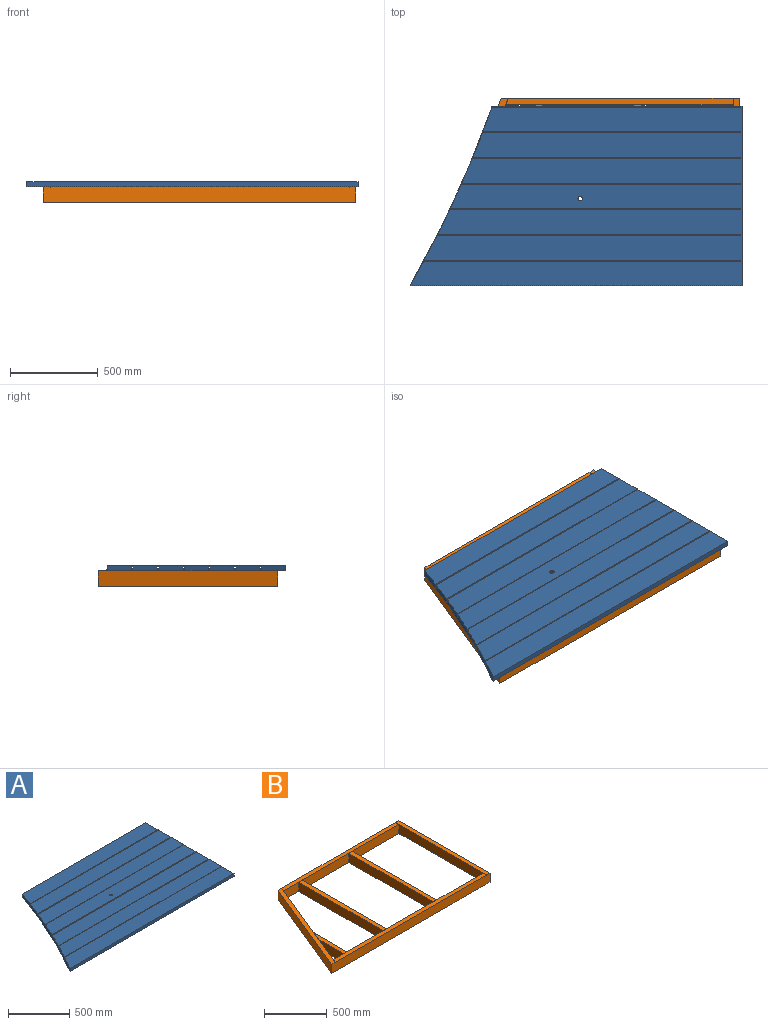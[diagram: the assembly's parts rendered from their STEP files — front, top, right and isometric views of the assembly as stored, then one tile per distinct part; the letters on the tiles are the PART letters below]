
ASSEMBLY  parts=2 mates=1
PART A: 33 faces, bbox 1890x1022.4x29.4 mm
  f0: cylinder r=6096mm len=1022.35mm, axis (0,0,-1), area 31985.5mm2, adj f1,f3,f4,f5,f6,f7,f8,f9
  f1: plane 1890x1022.35mm, normal (0,0,-1), area 1673082.8mm2, adj f0,f2,f10,f31,f32
  f2: plane 1022.35x29.37mm, normal (1,0,0), area 29037.2mm2, adj f1,f3,f4,f5,f6,f7,f8,f9
  f3: plane 1475.36x139.7mm, normal (0,0,1), area 202498.6mm2, adj f0,f2,f28,f30
  f4: plane 1532.89x139.7mm, normal (0,0,1), area 210247.9mm2, adj f0,f2,f25,f27
  f5: plane 1594.83x139.7mm, normal (0,0,1), area 218604.7mm2, adj f0,f2,f22,f24
  f6: plane 1661.33x139.7mm, normal (0,0,1), area 227082mm2, adj f0,f2,f19,f21,f32
  f7: plane 1732.57x139.7mm, normal (0,0,1), area 237222mm2, adj f0,f2,f16,f18
  f8: plane 1808.72x139.7mm, normal (0,0,1), area 247529.5mm2, adj f0,f2,f13,f15
  f9: plane 1890x139.7mm, normal (0,0,1), area 258539.2mm2, adj f0,f2,f10,f12
  f10: plane 1890x29.37mm, normal (0,-1,0), area 55507mm2, adj f0,f1,f2,f9
  f11: plane 1812.15x6.35mm, normal (0,0,1), area 11496.2mm2, adj f0,f2,f12,f13
  f12: plane 1812.15x22.23mm, normal (0,1,0), area 40274.9mm2, adj f0,f2,f9,f11
  f13: plane 1808.72x22.23mm, normal (0,-1,0), area 40198.8mm2, adj f0,f2,f8,f11
  f14: plane 1735.78x6.35mm, normal (0,0,1), area 11012mm2, adj f0,f2,f15,f16
  f15: plane 1735.78x22.23mm, normal (0,1,0), area 38577.6mm2, adj f0,f2,f8,f14
  f16: plane 1732.57x22.23mm, normal (0,-1,0), area 38506.3mm2, adj f0,f2,f7,f14
  f17: plane 1664.33x6.35mm, normal (0,0,1), area 10559mm2, adj f0,f2,f18,f19
  f18: plane 1664.33x22.23mm, normal (0,1,0), area 36989.8mm2, adj f0,f2,f7,f17
  f19: plane 1661.33x22.23mm, normal (0,-1,0), area 36923.1mm2, adj f0,f2,f6,f17
  f20: plane 1597.62x6.35mm, normal (0,0,1), area 10136mm2, adj f0,f2,f21,f22
  f21: plane 1597.62x22.23mm, normal (0,1,0), area 35507.2mm2, adj f0,f2,f6,f20
  f22: plane 1594.83x22.23mm, normal (0,-1,0), area 35445.1mm2, adj f0,f2,f5,f20
  f23: plane 1535.49x6.35mm, normal (0,0,1), area 9742.1mm2, adj f0,f2,f24,f25
  f24: plane 1535.49x22.23mm, normal (0,1,0), area 34126.2mm2, adj f0,f2,f5,f23
  f25: plane 1532.89x22.23mm, normal (0,-1,0), area 34068.4mm2, adj f0,f2,f4,f23
  f26: plane 1477.77x6.35mm, normal (0,0,1), area 9376.2mm2, adj f0,f2,f27,f28
  f27: plane 1477.77x22.23mm, normal (0,1,0), area 32843.4mm2, adj f0,f2,f4,f26
  f28: plane 1475.36x22.23mm, normal (0,-1,0), area 32789.8mm2, adj f0,f2,f3,f26
  f29: plane 1424.34x6.35mm, normal (0,0,1), area 9037.5mm2, adj f0,f2,f30,f31
  f30: plane 1424.34x22.23mm, normal (0,1,0), area 31655.9mm2, adj f0,f2,f3,f29
  f31: plane 1422.11x7.14mm, normal (0,1,0), area 10159.2mm2, adj f0,f1,f2,f29
  f32: cylinder r=12.7mm len=29.37mm, axis (0,0,1), area 2343.5mm2, adj f1,f6
PART B: 42 faces, bbox 1778x1022.4x88.9 mm
  f0: plane 1358.9x88.9mm, normal (0,1,0), area 120806.1mm2, adj f10,f11,f12,f13,f15,f17,f19,f21
  f1: plane 1295.24x88.9mm, normal (0,-1,0), area 108566.2mm2, adj f2,f3,f4,f6,f10,f15,f17,f21
  f2: plane 946.15x88.9mm, normal (-1,0,0), area 84112.6mm2, adj f1,f8,f16,f21,f24,f25,f26,f27
  f3: plane 946.15x88.9mm, normal (-1,0,0), area 84112.6mm2, adj f1,f9,f16,f21,f34,f35,f36,f37
  f4: plane 946.15x88.9mm, normal (1,0,0), area 84112.6mm2, adj f1,f9,f16,f21,f34,f35,f36,f37
  f5: plane 367.55x88.9mm, normal (1,0,0), area 32674.7mm2, adj f7,f15,f16,f21,f28,f29,f30,f31
  f6: plane 946.15x88.9mm, normal (1,0,0), area 84112.6mm2, adj f1,f8,f16,f21,f24,f25,f26,f27
  f7: plane 367.45x38.1mm, normal (0,0,1), area 12229.5mm2, adj f5,f18,f29,f31
  f8: plane 946.1x38.1mm, normal (0,0,1), area 36046.4mm2, adj f2,f6,f25,f27
  f9: plane 946.1x38.1mm, normal (0,0,1), area 36046.4mm2, adj f3,f4,f35,f37
  f10: plane 1295.19x38.1mm, normal (0,0,1), area 49049.2mm2, adj f0,f1,f33,f41
  f11: plane 1022.35x460.28mm, normal (0,0,1), area 42097.4mm2, adj f0,f13,f14,f15
  f12: plane 1022.35x38.1mm, normal (0,0,1), area 38951.5mm2, adj f0,f14,f17,f19
  f13: plane 1022.35x419.1mm, normal (-0.93,0.38,0), area 98227.2mm2, adj f0,f11,f14,f21
  f14: plane 1778x88.9mm, normal (0,-1,0), area 158064.1mm2, adj f11,f12,f13,f15,f17,f19,f20,f21
  f15: plane 1022.35x419.1mm, normal (0.93,-0.38,0), area 82440.5mm2, adj f0,f1,f5,f11,f14,f16,f18,f21
  f16: plane 1683.1x88.9mm, normal (0,1,0), area 139756.9mm2, adj f2,f3,f4,f5,f6,f15,f17,f18
  f17: plane 1022.35x88.9mm, normal (-1,0,0), area 84306.3mm2, adj f0,f1,f12,f14,f16,f21,f22,f32
  f18: plane 274.61x88.9mm, normal (-1,0,0), area 24412.2mm2, adj f7,f15,f16,f21,f28,f29,f30,f31
  f19: plane 1022.35x88.9mm, normal (1,0,0), area 90886.9mm2, adj f0,f12,f14,f21
  f20: plane 1698.67x38.1mm, normal (0,0,1), area 64421.8mm2, adj f14,f16,f23,f39
  f21: plane 1778x1022.35mm, normal (0,0,-1), area 278853.5mm2, adj f0,f1,f2,f3,f4,f5,f6,f13
  f22: plane 38.1x0.03mm, normal (0,0,1), area 1mm2, adj f14,f16,f17,f23
  f23: plane 38.1x2.54mm, normal (1,0,0), area 96.8mm2, adj f14,f16,f20,f22
  f24: plane 38.1x0.03mm, normal (0,0,1), area 1mm2, adj f1,f2,f6,f25
  f25: plane 38.1x2.54mm, normal (0,1,0), area 96.8mm2, adj f2,f6,f8,f24
  f26: plane 38.1x0.03mm, normal (0,0,1), area 1mm2, adj f2,f6,f16,f27
  f27: plane 38.1x2.54mm, normal (0,-1,0), area 96.8mm2, adj f2,f6,f8,f26
  f28: plane 93.01x38.1mm, normal (0,0,1), area 2.6mm2, adj f5,f15,f18,f29
  f29: plane 92.94x38.1mm, normal (-0.93,0.38,0), area 255.1mm2, adj f5,f7,f18,f28
  f30: plane 38.1x0.03mm, normal (0,0,1), area 1mm2, adj f5,f16,f18,f31
  f31: plane 38.1x2.54mm, normal (0,-1,0), area 96.8mm2, adj f5,f7,f18,f30
  f32: plane 38.1x0.03mm, normal (0,0,1), area 1mm2, adj f0,f1,f17,f33
  f33: plane 38.1x2.54mm, normal (1,0,0), area 96.8mm2, adj f0,f1,f10,f32
  f34: plane 38.1x0.03mm, normal (0,0,1), area 1mm2, adj f1,f3,f4,f35
  f35: plane 38.1x2.54mm, normal (0,1,0), area 96.8mm2, adj f3,f4,f9,f34
  f36: plane 38.1x0.03mm, normal (0,0,1), area 1mm2, adj f3,f4,f16,f37
  f37: plane 38.1x2.54mm, normal (0,-1,0), area 96.8mm2, adj f3,f4,f9,f36
  f38: plane 38.1x15.65mm, normal (0,0,1), area 1mm2, adj f14,f15,f16,f39
  f39: plane 38.1x15.62mm, normal (-0.93,0.38,0), area 104.6mm2, adj f14,f16,f20,f38
  f40: plane 38.1x15.65mm, normal (0,0,1), area 1mm2, adj f0,f1,f15,f41
  f41: plane 38.1x15.62mm, normal (-0.93,0.38,0), area 104.6mm2, adj f0,f1,f10,f40
PLACE A t=(41.54,267.89,88.9)mm
PLACE B t=(-523.24,-703.66,0)mm
MATE fastened B.f12 <-> A.f1  axis (0,0,1) through (0,511.18,88.9)mm
